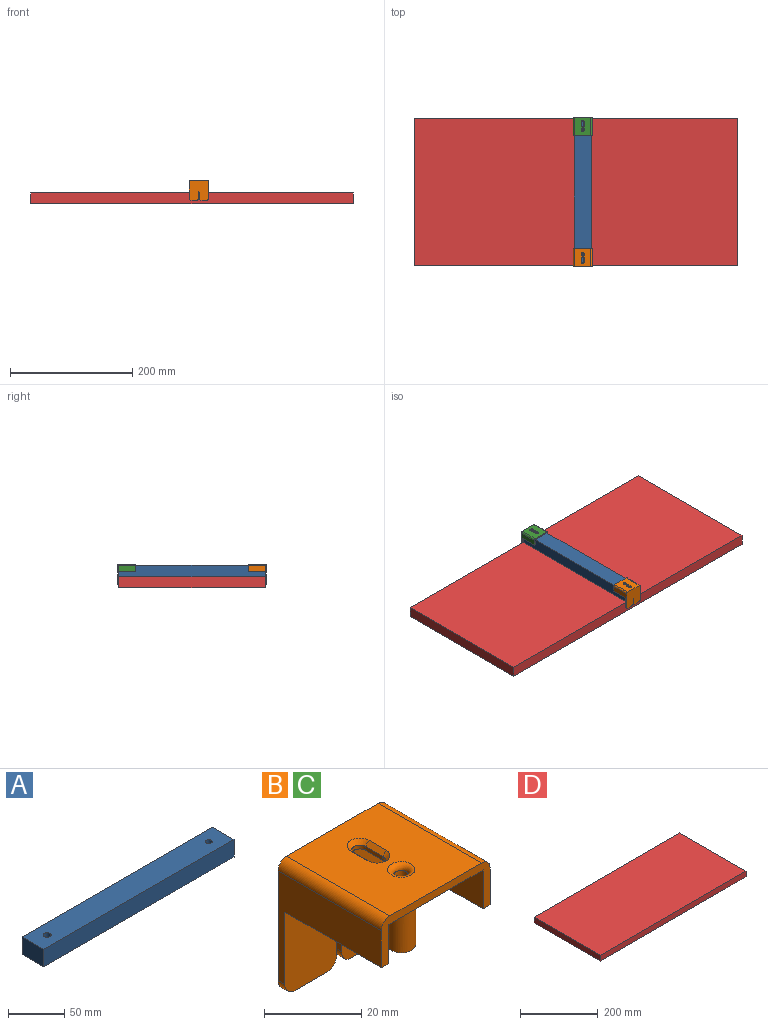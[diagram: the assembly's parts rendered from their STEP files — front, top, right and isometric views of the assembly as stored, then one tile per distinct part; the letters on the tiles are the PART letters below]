
ASSEMBLY  parts=4 mates=3
PART A: 8 faces, bbox 240x27.4x19 mm
  f0: plane 240x19mm, normal (0,1,0), area 4560mm2, adj f1,f3,f4,f5
  f1: plane 27.4x19mm, normal (-1,0,0), area 520.6mm2, adj f0,f2,f4,f5
  f2: plane 240x19mm, normal (0,-1,0), area 4560mm2, adj f1,f3,f4,f5
  f3: plane 27.4x19mm, normal (1,0,0), area 520.6mm2, adj f0,f2,f4,f5
  f4: plane 240x27.4mm, normal (0,0,1), area 6508.6mm2, adj f0,f1,f2,f3,f6,f7
  f5: plane 240x27.4mm, normal (0,0,-1), area 6508.6mm2, adj f0,f1,f2,f3,f6,f7
  f6: cylinder r=3mm len=19mm, axis (0,0,-1), area 358.1mm2, adj f4,f5
  f7: cylinder r=3.53mm len=19mm, axis (0,0,-1), area 421.1mm2, adj f4,f5
PART B: 34 faces, bbox 31.6x30x33 mm
  f0: plane 33x31.55mm, normal (0,1,0), area 1013.2mm2, adj f2,f5,f6,f9,f10,f11,f12,f18
  f1: plane 31.55x31mm, normal (0,-1,0), area 913.6mm2, adj f2,f3,f4,f5,f6,f8,f10,f13
  f2: plane 9.13x2mm, normal (0,0,-1), area 18.2mm2, adj f0,f1,f19,f22
  f3: plane 28x9.8mm, normal (1,0,0), area 274.4mm2, adj f1,f7,f8,f14
  f4: plane 28x9.8mm, normal (-1,0,0), area 274.4mm2, adj f1,f7,f8,f13
  f5: plane 30x27.5mm, normal (1,0,0), area 315.4mm2, adj f0,f1,f7,f11,f13,f18
  f6: plane 30x27.5mm, normal (-1,0,0), area 315.4mm2, adj f0,f1,f7,f12,f14,f19
  f7: plane 31.55x11.8mm, normal (0,-1,0), area 99.6mm2, adj f3,f4,f5,f6,f8,f9,f11,f12
  f8: plane 28x27.55mm, normal (0,0,-1), area 718.1mm2, adj f1,f3,f4,f7,f15,f24,f25,f26
  f9: plane 30x26.55mm, normal (0,0,1), area 723.3mm2, adj f0,f7,f11,f12,f28,f29,f30,f31
  f10: plane 9.13x2mm, normal (0,0,-1), area 18.2mm2, adj f0,f1,f18,f23
  f11: cylinder r=2.5mm len=30mm, axis (0,1,0), area 117.8mm2, adj f0,f5,f7,f9
  f12: cylinder r=2.5mm len=30mm, axis (0,-1,0), area 117.8mm2, adj f0,f6,f7,f9
  f13: plane 28x2mm, normal (0,0,-1), area 56mm2, adj f1,f4,f5,f7
  f14: plane 28x2mm, normal (0,0,-1), area 56mm2, adj f1,f3,f6,f7
  f15: cylinder r=3mm len=16.8mm, axis (0,0,1), area 316.7mm2, adj f8,f17
  f16: cylinder r=1.5mm len=17.5mm, axis (0,0,1), area 164.9mm2, adj f17,f32
  f17: plane 6x6mm, normal (0,0,-1), area 21.2mm2, adj f15,f16
  f18: cylinder r=3mm len=3mm, axis (0,-1,0), area 9.4mm2, adj f0,f1,f5,f10
  f19: cylinder r=3mm len=3mm, axis (0,1,0), area 9.4mm2, adj f0,f1,f2,f6
  f20: plane 10x2mm, normal (1,0,0), area 20mm2, adj f0,f1,f22,f33
  f21: plane 10x2mm, normal (-1,0,0), area 20mm2, adj f0,f1,f23,f33
  f22: cylinder r=3mm len=3mm, axis (0,-1,0), area 9.4mm2, adj f0,f1,f2,f20
  f23: cylinder r=3mm len=3mm, axis (0,1,0), area 9.4mm2, adj f0,f1,f10,f21
  f24: cylinder r=1.65mm len=3.3mm, axis (0,0,1), area 5.2mm2, adj f8,f25,f27,f31
  f25: plane 5x1mm, normal (1,0,0), area 5mm2, adj f8,f24,f26,f30
  f26: cylinder r=1.65mm len=3.3mm, axis (0,0,1), area 5.2mm2, adj f8,f25,f27,f28
  f27: plane 5x1mm, normal (-1,0,0), area 5mm2, adj f8,f24,f26,f29
  f28: cone r=1.65mm half-angle=45deg, axis (0,0,1), area 9.6mm2, adj f9,f26,f29,f30
  f29: plane 5x1mm, normal (-0.71,0,0.71), area 7.1mm2, adj f9,f27,f28,f31
  f30: plane 5x1mm, normal (0.71,0,0.71), area 7.1mm2, adj f9,f25,f28,f31
  f31: cone r=1.65mm half-angle=45deg, axis (0,0,1), area 9.6mm2, adj f9,f24,f29,f30
  f32: torus R=2.8mm, axis (0,0,1), area 25.3mm2, adj f9,f16
  f33: cylinder r=0.65mm len=2mm, axis (0,1,0), area 4.1mm2, adj f0,f1,f20,f21
PART C: same geometry as B
PART D: 6 faces, bbox 529x240x18 mm
  f0: plane 529x18mm, normal (0,1,0), area 9522mm2, adj f1,f3,f4,f5
  f1: plane 240x18mm, normal (-1,0,0), area 4320mm2, adj f0,f2,f4,f5
  f2: plane 529x18mm, normal (0,-1,0), area 9522mm2, adj f1,f3,f4,f5
  f3: plane 240x18mm, normal (1,0,0), area 4320mm2, adj f0,f2,f4,f5
  f4: plane 529x240mm, normal (0,0,1), area 126960mm2, adj f0,f1,f2,f3
  f5: plane 529x240mm, normal (0,0,-1), area 126960mm2, adj f0,f1,f2,f3
PLACE A rot(axis=(0,0,1),90deg) t=(23.36,-60.83,-37.99)mm fixed
PLACE B rot(axis=(0,0,1),180deg) t=(23.36,-180.83,-28.14)mm
PLACE C t=(23.36,59.17,-28.14)mm
PLACE D t=(14.79,-49.89,-55.99)mm
MATE slider A.f0 <-> D.f1  axis (-1,0,0) through (9.66,-60.83,-37.99)mm
MATE fastened A.f4 <-> C.f8  axis (0,0,1) through (23.36,59.17,-18.99)mm
MATE fastened B.f8 <-> A.f4  axis (0,0,-1) through (23.36,-180.83,-18.99)mm
